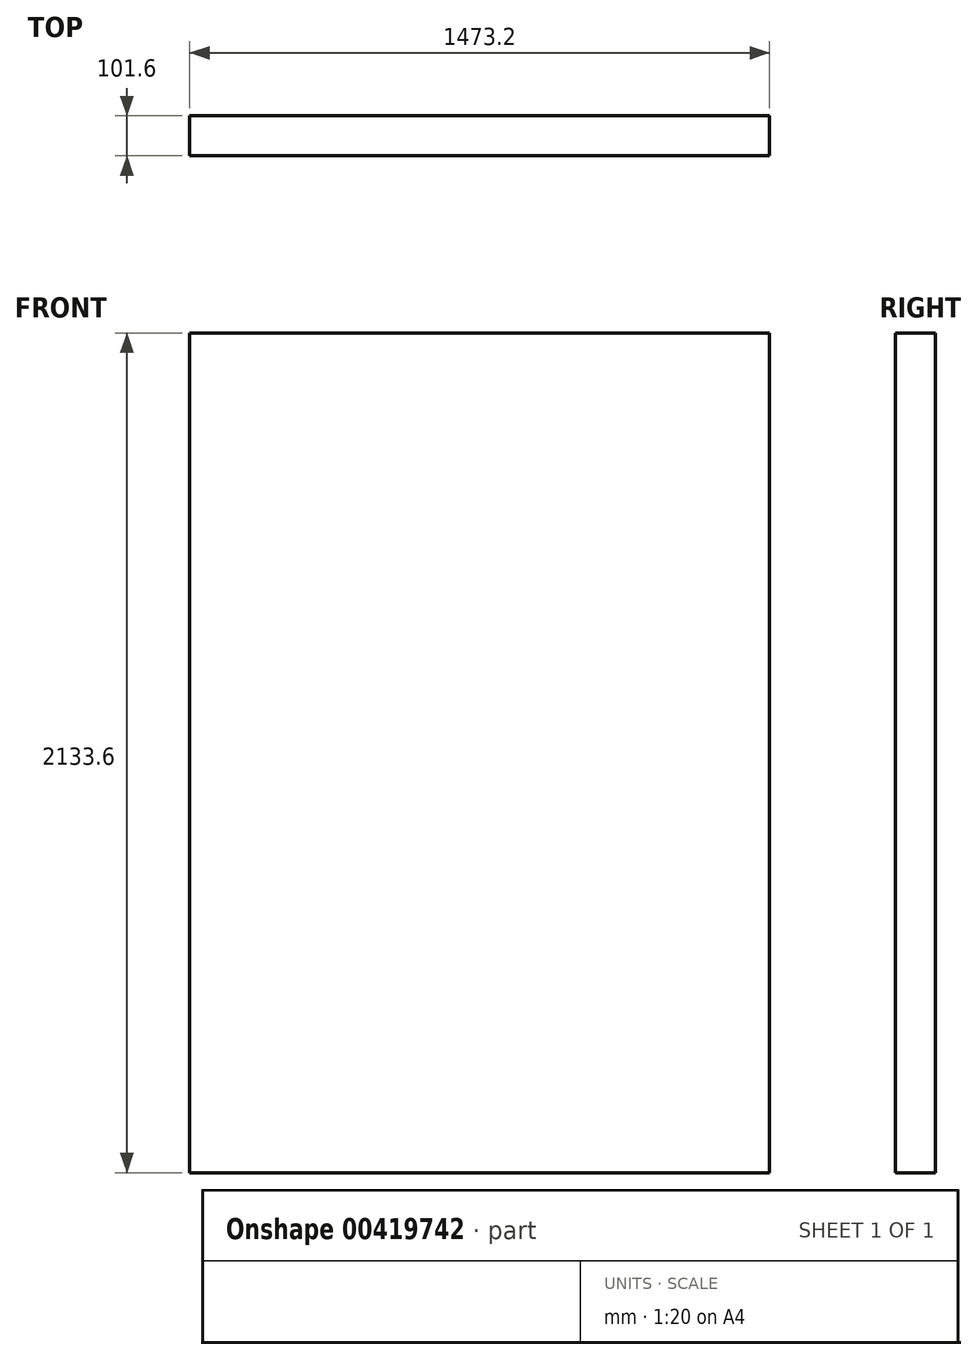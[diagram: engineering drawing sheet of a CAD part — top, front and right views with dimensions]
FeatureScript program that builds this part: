
annotation { "Feature Type Name" : "Feature", "Feature Type Description" : "" }
export const myFeature = defineFeature(function(context is Context, id is Id, definition is map)
    precondition{}
    {
        {
            var Q0;
            Q0=qCreatedBy(makeId("Front.planeOp"),FACE);
            var sketch = newSketch(context, id + "F0", { "sketchPlane" : qUnion([Q0])});
            skLineSegment(sketch, "E0", {"start": v(-784.3, 510.21) * mm, "end": v(-784.3, -1623.39) * mm});
            skLineSegment(sketch, "E1", {"start": v(-784.3, -1623.39) * mm, "end": v(688.9, -1623.39) * mm});
            skLineSegment(sketch, "E2", {"start": v(688.9, -1623.39) * mm, "end": v(688.9, 510.21) * mm});
            skLineSegment(sketch, "E3", {"start": v(688.9, 510.21) * mm, "end": v(-784.3, 510.21) * mm});
            skSolve(sketch);
        }
        {
            var Q0;
            Q0 = qSketchRegion(id + "F0", true);
            extrude(context, id + "F1", {"entities" : qUnion([Q0]), "depth" : 101.6 * mm});
        }
    });
